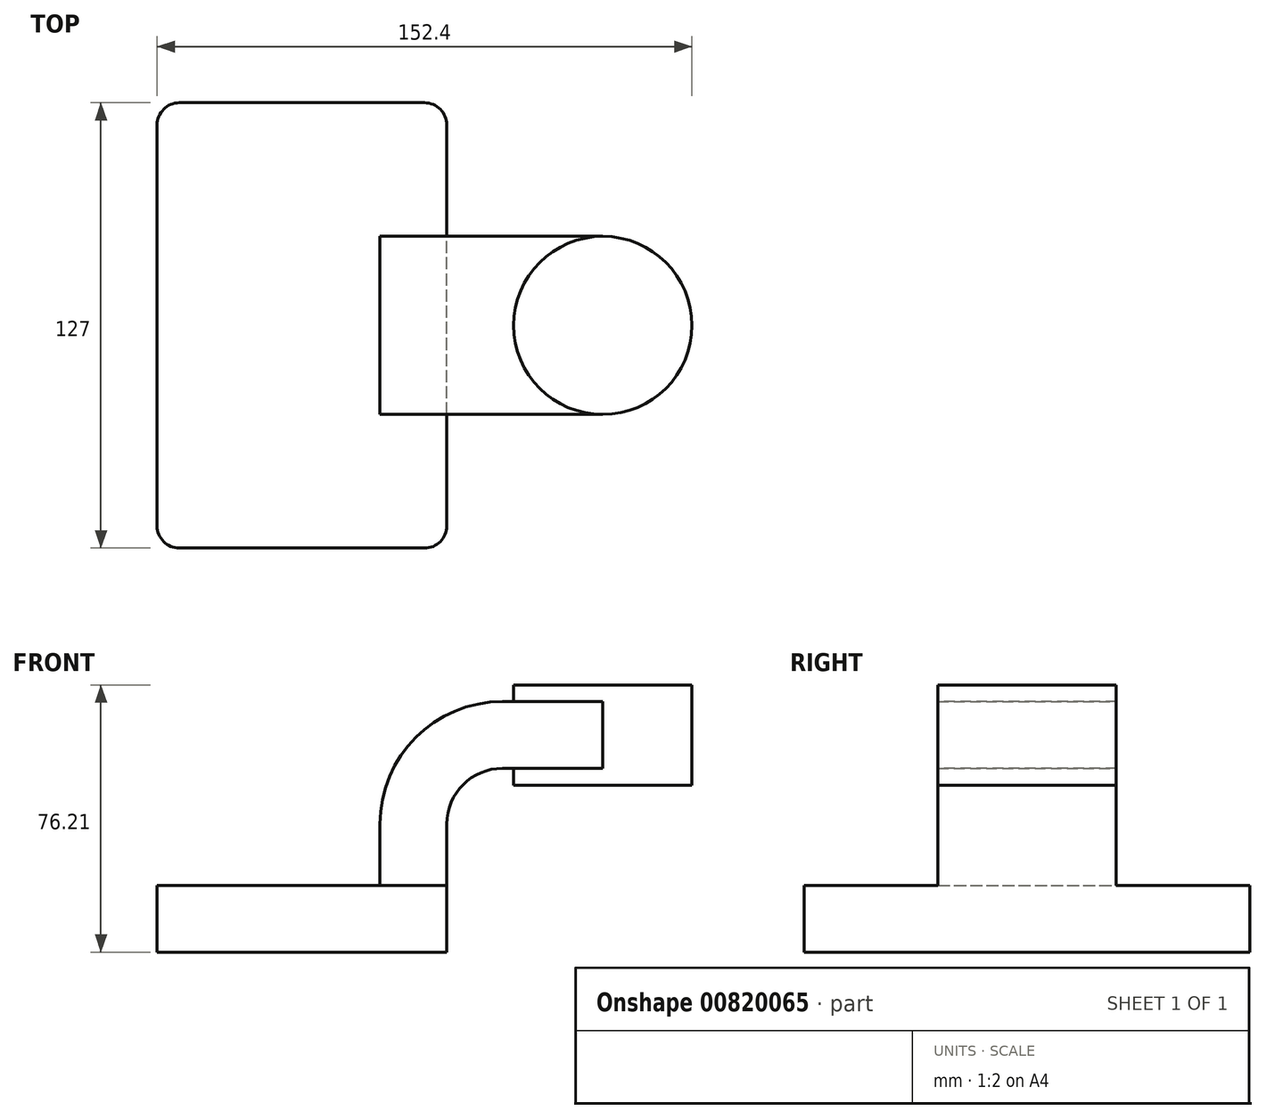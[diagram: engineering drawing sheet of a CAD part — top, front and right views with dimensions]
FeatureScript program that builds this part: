
annotation { "Feature Type Name" : "Feature", "Feature Type Description" : "" }
export const myFeature = defineFeature(function(context is Context, id is Id, definition is map)
    precondition{}
    {
        {
            var Q0;
            Q0=qCreatedBy(makeId("Front.planeOp"),FACE);
            var sketch = newSketch(context, id + "F0", { "sketchPlane" : qUnion([Q0])});
            skLineSegment(sketch, "E0.bottom", {"start": v(41.28, -9.52) * mm, "end": v(-41.28, -9.53) * mm});
            skLineSegment(sketch, "E0.top", {"start": v(41.28, 9.53) * mm, "end": v(-41.28, 9.53) * mm});
            skLineSegment(sketch, "E0.left", {"start": v(41.28, -9.52) * mm, "end": v(41.28, 9.53) * mm});
            skLineSegment(sketch, "E0.right", {"start": v(-41.28, -9.53) * mm, "end": v(-41.28, 9.53) * mm});
            skPoint(sketch, "E0.middle", {"position": v(0, 0) * mm});
            skLineSegment(sketch, "E1.bottom", {"start": v(111.12, 38.1) * mm, "end": v(60.32, 38.1) * mm});
            skLineSegment(sketch, "E1.top", {"start": v(111.12, 66.68) * mm, "end": v(60.32, 66.68) * mm});
            skLineSegment(sketch, "E1.left", {"start": v(111.12, 38.1) * mm, "end": v(111.12, 66.68) * mm});
            skLineSegment(sketch, "E1.right", {"start": v(60.32, 38.1) * mm, "end": v(60.32, 66.68) * mm});
            skPoint(sketch, "E1.middle", {"position": v(85.72, 52.39) * mm});
            skLineSegment(sketch, "E2", {"start": v(41.28, 9.53) * mm, "end": v(41.28, 27) * mm});
            skArc(sketch, "E3", {"start": v(41.27, 27) * mm, "mid": v(45.92, 38.23) * mm, "end": v(57.15, 42.88) * mm});
            skLineSegment(sketch, "E4", {"start": v(57.15, 42.88) * mm, "end": v(85.7, 42.88) * mm});
            skLineSegment(sketch, "E5.0", {"start": v(57.15, 61.93) * mm, "end": v(85.72, 61.93) * mm});
            skArc(sketch, "E5.1", {"start": v(22.23, 27) * mm, "mid": v(32.45, 51.7) * mm, "end": v(57.15, 61.93) * mm});
            skLineSegment(sketch, "E5.2", {"start": v(22.22, 9.53) * mm, "end": v(22.22, 27) * mm});
            skLineSegment(sketch, "E6", {"start": v(85.7, 42.88) * mm, "end": v(85.72, 61.93) * mm});
            skFitSpline(sketch, "E7", {"points": [v(-41.28, 9.52) * mm, v(57.15, 61.93) * mm], "startDerivative": vector(47.27, 81.32) * mm, "endDerivative": vector(161.4, -0.53) * mm});
            skPoint(sketch, "E8", {"position": v(85.72, 66.68) * mm});
            skLineSegment(sketch, "E9", {"start": v(85.72, 66.68) * mm, "end": v(85.72, 38.1) * mm});
            skSolve(sketch);
        }
        {
            var Q0;
            Q0=makeQuery(id+"F0.imprint","IMPRINT",FACE,{"disambiguationData":[TD([[makeQuery(id+"F0.imprint","IMPRINT",EDGE,{"derivedFrom":sQuery(id+"F0.wireOp",EDGE,"E0.bottom")}),-1.0]])]});
            extrude(context, id + "F1", {"entities" : qUnion([Q0]), "endBound" : BoundingType.SYMMETRIC, "depth" : 127 * mm, "offsetDistance" : 25.4 * mm});
        }
        {
            var Q0;
            {var subQ1=sQuery(id+"F0.wireOp",EDGE,"E2");Q0=makeQuery(id+"F0.imprint","IMPRINT",FACE,{"disambiguationData":[TD([[makeQuery(id+"F0.imprint","IMPRINT",EDGE,{"derivedFrom":subQ1}),1.0]])]});}
            var Q1;
            {var subQ5=sQuery(id+"F0.wireOp",EDGE,"E6");Q1=makeQuery(id+"F0.imprint","IMPRINT",FACE,{"disambiguationData":[TD([[makeQuery(id+"F0.imprint","IMPRINT",EDGE,{"derivedFrom":subQ5}),1.0]])]});}
            extrude(context, id + "F2", {"entities" : qUnion([Q0, Q1]), "operationType" : NewBodyOperationType.ADD, "endBound" : BoundingType.SYMMETRIC, "depth" : 50.8 * mm, "offsetDistance" : 25.4 * mm});
        }
        {
            var Q0;
            Q0=makeQuery(id+"F0.imprint","IMPRINT",FACE,{"disambiguationData":[TD([[makeQuery(id+"F0.imprint","IMPRINT",EDGE,{"derivedFrom":sQuery(id+"F0.wireOp",EDGE,"E5.1")}),1.0]])]});
            extrude(context, id + "F3", {"entities" : qUnion([Q0]), "operationType" : NewBodyOperationType.ADD, "endBound" : BoundingType.SYMMETRIC, "depth" : 15.88 * mm, "offsetDistance" : 25.4 * mm});
        }
        {
            var Q0;
            {var subQ4=sQuery(id+"F0.wireOp",EDGE,"E1.left");Q0=makeQuery(id+"F0.imprint","IMPRINT",FACE,{"disambiguationData":[TD([[makeQuery(id+"F0.imprint","IMPRINT",EDGE,{"derivedFrom":subQ4}),1.0]])]});}
            var Q1;
            Q1=sQuery(id+"F0.wireOp",EDGE,"E9");
            revolve(context, id + "F4", {"operationType" : NewBodyOperationType.ADD, "surfaceOperationType" : NewSurfaceOperationType.NEW, "entities" : qUnion([Q0]), "axis" : qUnion([Q1]), "revolveType" : RevolveType.FULL});
        }
        {
            var Q0;
            Q0=makeQuery(id+"F1.opExtrude","CAP_EDGE",EDGE,{"disambiguationData":[OSD([sQuery(id+"F0.wireOp",EDGE,"E0.left")])],"isStart":false});
            var Q1;
            Q1=makeQuery(id+"F1.opExtrude","CAP_EDGE",EDGE,{"disambiguationData":[OSD([sQuery(id+"F0.wireOp",EDGE,"E0.left")])],"isStart":true});
            var Q2;
            Q2=makeQuery(id+"F1.opExtrude","CAP_EDGE",EDGE,{"disambiguationData":[OSD([sQuery(id+"F0.wireOp",EDGE,"E0.right")])],"isStart":false});
            var Q3;
            Q3=makeQuery(id+"F1.opExtrude","CAP_EDGE",EDGE,{"disambiguationData":[OSD([sQuery(id+"F0.wireOp",EDGE,"E0.right")])],"isStart":true});
            fillet(context, id + "F5", {"entities" : qUnion([Q0, Q1, Q2, Q3]), "radius" : 6.35 * mm, "tangentPropagation" : true, "allowEdgeOverflow" : false});
        }
    });
